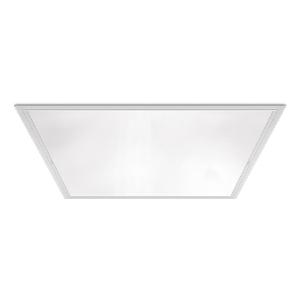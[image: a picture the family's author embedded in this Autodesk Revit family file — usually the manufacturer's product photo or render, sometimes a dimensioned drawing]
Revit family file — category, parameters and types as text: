
# Revit family: 3f_filippi_-_l_600_luce_diffusa_lgs_3f_filippi_-_22821_-_l_600_28w-840_dali_lgs_596x596
name_source: partatom
category: Lighting Fixtures
units: mm (PartAtom-declared; Revit-internal decimal feet)

## family parameters
Cut with Voids When Loaded = No
Host = Face
Light Source = No
Part Type = Normal
Room Calculation Point = No
Round Connector Dimension = Use Diameter
Shared = No

## types (1)
- 3F Filippi - L 600 Luce Diffusa LGS (1 x LED, 3978 lm, 32.5 W, 4000 K)
    Apparent Load = 33 VA
    Approval mark = ENEC
    CIE Flux Codes = 66 93 98 100 100
    Color Rendering = 80
    Color Temperature = 4000 K
    Control Gear = Electronic transformer
    Default Elevation = 1800 mm
    Description = ILLUMINOTECHNICAL
Luminous efficiency 100% (DLOR 100%, ULOR 0%).
Initial luminous flux of the luminaire 3978 lm.
Direct symmetric distribution.
Installation Interdistance Transv.D = 1.14 x hu - Long.D = 1.16 x hu.
Average luminance <1500 cd/m² for radial angles >65°.
Tabular UGR (CIE 117 - 4H-8H; S=0.25H; 70/50/20): RUG 16.6 - 16.5.
Beam angle: 85° - 85°.
Luminous efficacy 122 lm/W.
Lifetime (L93/B10): 30000 h. (tq+25°C)
Lifetime (L90/B10): 50000 h. (tq+25°C)
Lifetime (L85/B10): 80000 h. (tq+25°C)
Lifetime (L80/B10): 100000 h. (tq+25°C)
Sudden decreased luminous flux after 50000 hours: 0% (C0).
Photobiological safety in compliance with IEC/TR 62778: RG0 risk exempt, (IEC 62471).
In compliance with IEC/EN 62722-2-1 - IEC/EN 62717 standards.

SOURCE
Squared LED module 28W/840.
Source with special protection against aggressive chemically-volatile substances for standard LED technology.
Energy efficiency class (UE 2019/2020 - UE 2019/2015): D.
CIE 13.3 Colour rendering index: CRI >80 (R9 <50%).
IES TM-30 Fidelity Index: Rf = 84 Rg = 95.
CCT nominal colour temperature 4000 K.
Colour initial tolerance (MacAdam): SDCM 3.

MECHANICAL
Housing in galvannealed steel, painted in white epoxy-polyester.
Perimetral frame in white polycarbonate.
LGS micro-prismatic flat diffuser in transparent methacrylate (PMMA), multi-lenticular exterior, anti-glare.
Anti-glare opal polycarbonate filter for brightness uniformity.
Luminaire with limited surface temperature. - D - (EN 60598-2-24)
Dimensions: 596x596 mm, height 95 mm. Weight 5.305 kg.
IP65 protection degree for exposed part, IP64 for recessed part.
Mechanical strength to impacts IK06 (1 joule).
Glow-wire test resistance 650°C.

ELECTRICAL
Halogen Free DALI-2, PUSH-DIM, electronic wiring 230V-50/60Hz, power factor 0.95 at full load, THD <25%, constant output current, class I, 1 driver, 1 DALI addresse.
Power of the luminaire 32.5 W.
CE - IEC 60598-1 - EN 60598-1.
SAFE FLICKER: PstLM=<1 and SVM=<0.4 (IEC TR 61547-1 and IEC TR 63158), to ensure a more comfortable and safe light.
Luminaire compliant with EN 60598-2-22 for power supply from a centralised emergency system CPSS (Central Power Supply System), not incorporated in the luminaire - high risk areas excluded. The default power and flux are 100% in AC and 15% in DC.
Ambient temperature from 0°C to +40°C.
Temperature class T6 max 85°C.
5-pole terminal block (L-N-PE-DA/DA) quick connection for line connection with connection capacity 2x2.5 mm² per poles.
Relative humidity UR: <85%.

INSTALLATION
Lay-on or pull-up recessed fitting using frame accessory.
All accessories dedicated to this product are available on the Catalog and on our website www.3F-Filippi.com.

APPLICATIONS
Suitable product for food production plants (HACCP), IFS (Food Version 6), BRC (GSFS Food Version 7).
In environments requiring protection and simplified cleaning.
Hospitals, pharmaceutical, chemical, aseptic laboratories, sterilised rooms.
Environments with VDTs.
Environments where demanding visual tasks are performed and soft diffuse light is required for optimal visual comfort and total shielding of the light source.

LIGHT MANAGEMENT
Recommended minimum setting: 10%.
The device, equipped with DALI-2 driver, can be controlled manually with 3F Easy Dim technology or automatically/manually with 3F Smart Dimming technology and/or centralised DALI systems.
DALI-2 certification guarantees interoperability with other devices with the same certification.
In electrical systems without a regulation system (manual or automatic) and DALI bus, a suitable jumper must be made on the DA-DA terminals of the appliance.

WARNING
Luminaire designed for disposal/recycling at end-of-life.
Replaceable (LED only) light source by a professional. Replaceable control gear by a professional.
    Height = 0 mm  [stored 0 ft]
    Lamp = 1 x LED
    Lamp Light Flux = 3978 lm
    Lamp Power = 32.5 W
    Lamp count = 1
    Length = 596 mm
    Lifetime = 50000 h
    Luminous efficacy = 122 lm/W
    Manufacturer = 3F Filippi
    ModVariant = No
    Model = 3F Filippi - 22821 - L 600 28W-840 DALI LGS 596x596
    Mounting Place = Ceiling
    Mounting Type = Recessed
    Number of Poles = 1
    OnlyDefault = Yes
    Power Factor = 1
    Product Name = 3F Filippi - L 600 Luce Diffusa LGS
    Product group = recessed luminaire
    ProductGroupID = 4
    Protection Class = Protection class I
    Protection Degree = IP 64
    RLX_Detail_Level = 1
    RLX_Emergency_Light_Flux = 0 lm
    RLX_Emergency_Type = 0
    RLX_Emergency_Type_DB = No
    RlxData = <blob elided: 129369 chars, md5=57a3484f>
    Socket = socket
    Standby Power = 0 W
    System Light Flux = 3978 lm
    System Power = 33 W
    Type Comments = Product without accessories
    Type Image = 3ffilippi_l_600_luce_diffusa_lgs.jpg
    URL = http://relux.com
    VarID = ---
    Voltage = 0 V
    Weight = 0.00 kg
    Width = 596 mm

note: [stored X ft] marks values corroborated as IEEE doubles in the binary element streams (Revit-internal decimal feet)

## geometry (parser evidence)
native form markers: Blend x4, Sweep x8
no freeform markers — native parametric forms only
